# Revit family: Faucet-Lavatory-American_Standard-Monterrey-6540.174.002
name_source: partatom
category: Plumbing Fixtures
units: mm (PartAtom-declared; Revit-internal decimal feet)

## family parameters
Always vertical = No
Cut with Voids When Loaded = No
OmniClass Number = 23.45.55.17
OmniClass Title = Mixing Faucets
Part Type = Normal
Room Calculation Point = No
Round Connector Dimension = Use Diameter
Shared = Yes
Work Plane-Based = Yes

## types (1)
- 6540.174.002
    ADA Compliant = Yes
    ASME A112.18.1/CSA B125.1 = Yes
    Assembly Code = D2020300
    CW Connection = Yes
    CWFU = 1.5
    CalGreen Compliant = Yes
    Cold Water Connection Diameter = 1/2"
    Default Elevation = 0"
    Description = Monterrey 0.35 gpm Two-handle 8" Widespread Lavatory Faucet Rigid/Swivel Gooseneck with 5" Reach
    Finish = Brass-American Standard-002-Polished Chrome
    Flow Rate = 0.35 gpm (1.3L/min)
    HW Connection = Yes
    HWFU = 1.5
    Handle Distance = 8"
    Height = 10 5/8"
    Hot Water Connection Diameter = 1/2"
    Installation Type = Deck Mounted
    Length = 15 3/4"
    Manufacturer = American Standard
    Material = Brass-American Standard-002-Polished Chrome
    Model = 6540.174.002
    Price = Prices may vary. Please consult Manufacturer Representative for most up-to-date price list.
    Product Documentation Link = https://americanstandard.box.com
    Product Page URL = https://www.americanstandard-us.com
    Reach Height = 6 1/2"
    Revised Date = 09/27/2021
    Spout Reach = 5"
    URL = http://www.americanstandard-us.com
    Vent Connection = No
    WFU = 2
    Warranty Information = 5 Year Limited Warranty for Commercial Installations
    Waste Connection = No

## geometry (parser evidence)
native form markers: Sweep x2
no freeform markers — native parametric forms only
